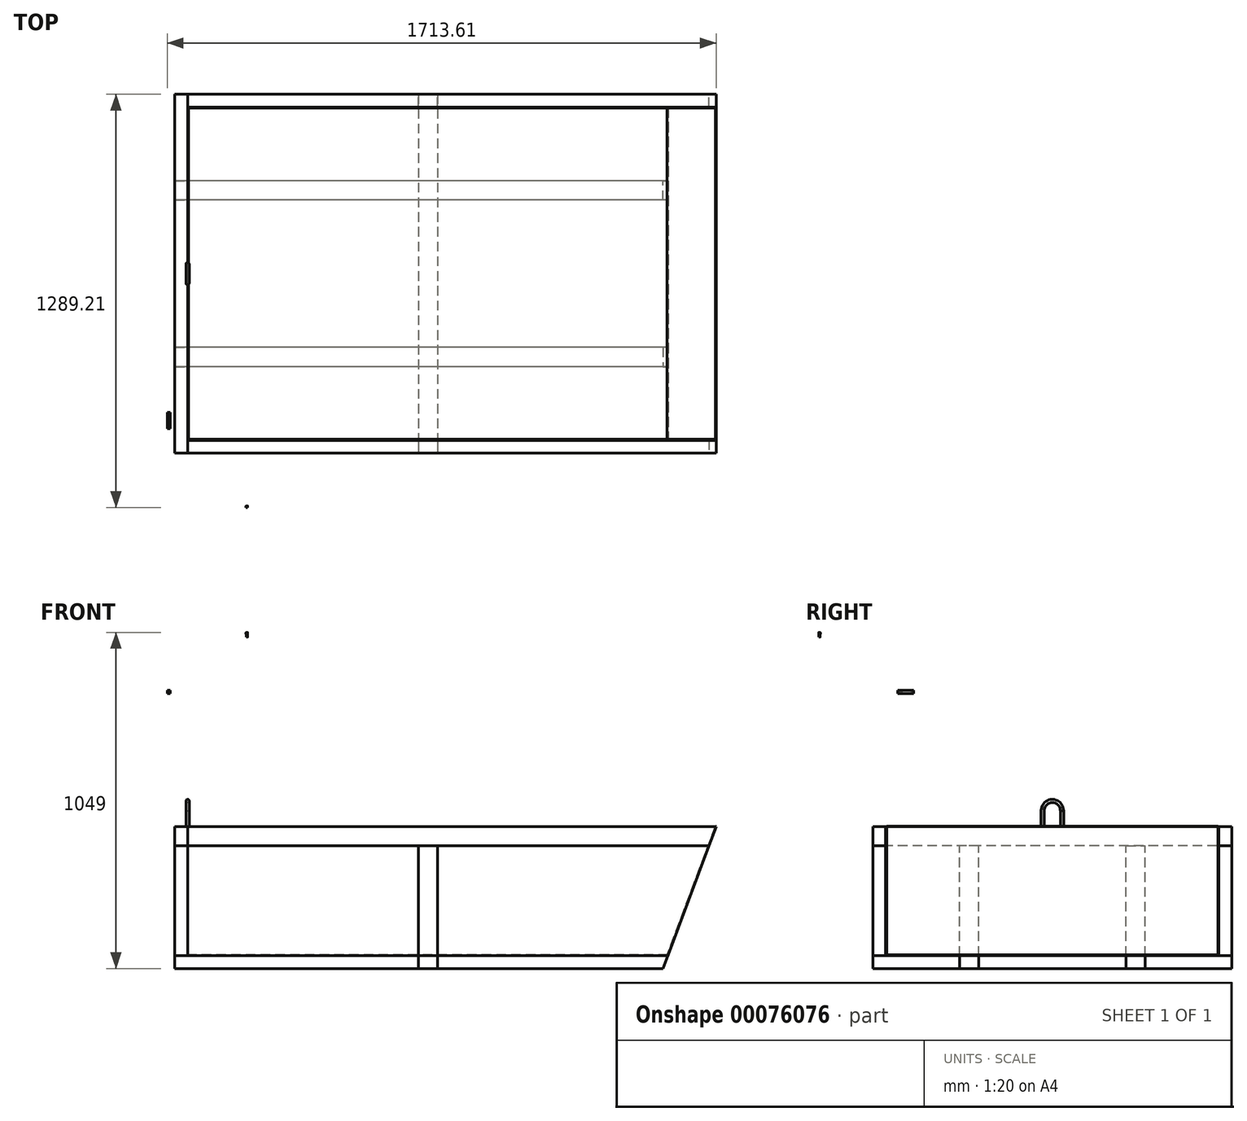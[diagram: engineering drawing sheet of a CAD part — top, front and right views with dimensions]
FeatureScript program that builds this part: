
annotation { "Feature Type Name" : "Feature", "Feature Type Description" : "" }
export const myFeature = defineFeature(function(context is Context, id is Id, definition is map)
    precondition{}
    {
        {
            var Q0;
            Q0=qCreatedBy(makeId("Top.planeOp"),FACE);
            var sketch = newSketch(context, id + "F0", { "sketchPlane" : qUnion([Q0])});
            skLineSegment(sketch, "E0.bottom", {"start": v(750, 520) * mm, "end": v(-750, 520) * mm});
            skLineSegment(sketch, "E0.top", {"start": v(750, -520) * mm, "end": v(-750, -520) * mm});
            skLineSegment(sketch, "E0.left", {"start": v(750, 520) * mm, "end": v(750, -520) * mm});
            skLineSegment(sketch, "E0.right", {"start": v(-750, 520) * mm, "end": v(-750, -520) * mm});
            skPoint(sketch, "E0.middle", {"position": v(0, 0) * mm});
            skSolve(sketch);
        }
        {
            var Q0;
            Q0 = qSketchRegion(id + "F0", true);
            extrude(context, id + "F1", {"entities" : qUnion([Q0]), "depth" : 3 * mm});
        }
        {
            var Q0;
            Q0=makeQuery(id+"F1.opExtrude","SWEPT_FACE",FACE,{"disambiguationData":[OSD([sQuery(id+"F0.wireOp",EDGE,"E0.top")])]});
            var sketch = newSketch(context, id + "F2", { "sketchPlane" : qUnion([Q0])});
            skLineSegment(sketch, "E1.0", {"start": v(750, 3) * mm, "end": v(-750, 3) * mm});
            skLineSegment(sketch, "E2", {"start": v(-750, 3) * mm, "end": v(-750, 403) * mm});
            skLineSegment(sketch, "E3", {"start": v(-750, 403) * mm, "end": v(900, 403) * mm});
            skLineSegment(sketch, "E4", {"start": v(900, 403) * mm, "end": v(750, 3) * mm});
            skSolve(sketch);
        }
        {
            var Q0;
            Q0 = qSketchRegion(id + "F2", true);
            extrude(context, id + "F3", {"entities" : qUnion([Q0]), "oppositeDirection" : true, "depth" : 3 * mm});
        }
        {
            var Q0;
            Q0=makeQuery(id+"F3.opExtrude","SWEPT_BODY",BODY,{"disambiguationData":[OSD([sQuery(id+"F2.wireOp",EDGE,"E1.0"),sQuery(id+"F2.wireOp",EDGE,"E2"),sQuery(id+"F2.wireOp",EDGE,"E3"),sQuery(id+"F2.wireOp",EDGE,"E4")])]});
            var Q1;
            Q1=qCreatedBy(makeId("Front.planeOp"),FACE);
            mirror(context, id + "F4", {"operationType" : NewBodyOperationType.ADD, "entities" : qUnion([Q0]), "mirrorPlane" : qUnion([Q1])});
        }
        {
            var Q0;
            {var subQ0=makeQuery(id+"F3.opExtrude","SWEPT_FACE",FACE,{"disambiguationData":[OSD([sQuery(id+"F2.wireOp",EDGE,"E2")])]});Q0=makeQuery(id+"F4.boolean.opBoolean","MERGE",FACE,{"derivedFrom":[makeQuery(id+"F1.opExtrude","SWEPT_FACE",FACE,{"disambiguationData":[OSD([sQuery(id+"F0.wireOp",EDGE,"E0.right")])]}),subQ0,makeQuery(id+"F4.opPattern","COPY",FACE,{"derivedFrom":subQ0,"instanceName":"1"})]});}
            var sketch = newSketch(context, id + "F5", { "sketchPlane" : qUnion([Q0])});
            skLineSegment(sketch, "E5.0", {"start": v(-517, 3) * mm, "end": v(-517, 403) * mm});
            skLineSegment(sketch, "E5.1", {"start": v(-517, 3) * mm, "end": v(517, 3) * mm});
            skLineSegment(sketch, "E5.2", {"start": v(517, 3) * mm, "end": v(517, 403) * mm});
            skLineSegment(sketch, "E6", {"start": v(-517, 403) * mm, "end": v(517, 403) * mm});
            skSolve(sketch);
        }
        {
            var Q0;
            Q0 = qSketchRegion(id + "F5", true);
            extrude(context, id + "F6", {"entities" : qUnion([Q0]), "oppositeDirection" : true, "depth" : 3 * mm});
        }
        {
            var Q0;
            Q0=makeQuery(id+"F3.opExtrude","SWEPT_FACE",FACE,{"disambiguationData":[OSD([sQuery(id+"F2.wireOp",EDGE,"E4")])]});
            var sketch = newSketch(context, id + "F7", { "sketchPlane" : qUnion([Q0])});
            skLineSegment(sketch, "E7.0", {"start": v(517, 266.15) * mm, "end": v(-517, 266.15) * mm});
            skLineSegment(sketch, "E7.1", {"start": v(-517, 693.35) * mm, "end": v(-517, 266.15) * mm});
            skLineSegment(sketch, "E7.2", {"start": v(517, 693.35) * mm, "end": v(517, 266.15) * mm});
            skLineSegment(sketch, "E8", {"start": v(-517, 693.35) * mm, "end": v(517, 693.35) * mm});
            skSolve(sketch);
        }
        {
            var Q0;
            Q0 = qSketchRegion(id + "F7", true);
            extrude(context, id + "F8", {"entities" : qUnion([Q0]), "oppositeDirection" : true, "depth" : 3 * mm});
        }
        {
            var Q0;
            Q0=makeQuery(id+"F4.boolean.opBoolean","MERGE",FACE,{"derivedFrom":[makeQuery(id+"F1.opExtrude","SWEPT_FACE",FACE,{"disambiguationData":[OSD([sQuery(id+"F0.wireOp",EDGE,"E0.top")])]}),makeQuery(id+"F3.opExtrude","CAP_FACE",FACE,{"disambiguationData":[OSD([sQuery(id+"F2.wireOp",EDGE,"E1.0"),sQuery(id+"F2.wireOp",EDGE,"E2"),sQuery(id+"F2.wireOp",EDGE,"E3"),sQuery(id+"F2.wireOp",EDGE,"E4")])],"isStart":true})]});
            cPlane(context, id + "F9", {"entities" : qUnion([Q0]), "cplaneType" : CPlaneType.OFFSET, "offset" : 40 * mm, "width" : 150 * mm, "height" : 150 * mm});
        }
        {
            var Q0;
            Q0=qCreatedBy(id+"F9.planeOp",FACE);
            var sketch = newSketch(context, id + "F10", { "sketchPlane" : qUnion([Q0])});
            skLineSegment(sketch, "E9.0", {"start": v(-750, 403) * mm, "end": v(-750, 343) * mm});
            skLineSegment(sketch, "E10", {"start": v(-750, 403) * mm, "end": v(-790, 403) * mm});
            skLineSegment(sketch, "E11", {"start": v(-790, 403) * mm, "end": v(-790, 343) * mm});
            skLineSegment(sketch, "E12", {"start": v(-790, 343) * mm, "end": v(-750, 343) * mm});
            skPoint(sketch, "E13.orphan", {"position": v(-750, 0) * mm});
            skSolve(sketch);
        }
        {
            var Q0;
            Q0 = qSketchRegion(id + "F10", true);
            extrude(context, id + "F11", {"entities" : qUnion([Q0]), "oppositeDirection" : true, "depth" : 1120 * mm});
        }
        {
            var Q0;
            Q0=makeQuery(id+"F11.opExtrude","SWEPT_FACE",FACE,{"disambiguationData":[OSD([sQuery(id+"F10.wireOp",EDGE,"E9.0")])]});
            var sketch = newSketch(context, id + "F12", { "sketchPlane" : qUnion([Q0])});
            skLineSegment(sketch, "E14.0", {"start": v(-520, 403) * mm, "end": v(-560, 403) * mm});
            skLineSegment(sketch, "E14.1", {"start": v(-560, 403) * mm, "end": v(-560, 343) * mm});
            skLineSegment(sketch, "E14.2", {"start": v(-520, 343) * mm, "end": v(-560, 343) * mm});
            skLineSegment(sketch, "E14.3", {"start": v(-520, 403) * mm, "end": v(-520, 343) * mm});
            skPoint(sketch, "E15.orphan", {"position": v(560, 403) * mm});
            skPoint(sketch, "E16.orphan", {"position": v(560, 343) * mm});
            skPoint(sketch, "E17.orphan", {"position": v(-520, 3) * mm});
            skSolve(sketch);
        }
        {
            var Q0;
            Q0=makeQuery(id+"F12.imprint","IMPRINT",FACE,{"disambiguationData":[TD([[makeQuery(id+"F12.imprint","IMPRINT",EDGE,{"derivedFrom":sQuery(id+"F12.wireOp",EDGE,"E14.0")}),1.0]])]});
            var Q1;
            Q1=makeQuery(id+"F8.opExtrude","CAP_FACE",FACE,{"disambiguationData":[OSD([sQuery(id+"F7.wireOp",EDGE,"E7.0"),sQuery(id+"F7.wireOp",EDGE,"E7.1"),sQuery(id+"F7.wireOp",EDGE,"E7.2"),sQuery(id+"F7.wireOp",EDGE,"E8")])],"isStart":true});
            extrude(context, id + "F13", {"entities" : qUnion([Q0]), "endBound" : BoundingType.UP_TO_SURFACE, "endBoundEntityFace" : qUnion([Q1]), "depth" : 25 * mm});
        }
        {
            var Q0;
            Q0=makeQuery(id+"F13.opExtrude","SWEPT_FACE",FACE,{"disambiguationData":[OSD([sQuery(id+"F12.wireOp",EDGE,"E14.2")])]});
            var sketch = newSketch(context, id + "F14", { "sketchPlane" : qUnion([Q0])});
            skLineSegment(sketch, "E18.0", {"start": v(30, 520) * mm, "end": v(-30, 520) * mm});
            skLineSegment(sketch, "E19", {"start": v(0, 520) * mm, "end": v(0, 560) * mm, "construction": true});
            skLineSegment(sketch, "E20", {"start": v(0, 560) * mm, "end": v(-30, 560) * mm});
            skLineSegment(sketch, "E21", {"start": v(-30, 560) * mm, "end": v(-30, 520) * mm});
            skLineSegment(sketch, "E22", {"start": v(0, 560) * mm, "end": v(30, 560) * mm});
            skLineSegment(sketch, "E23", {"start": v(30, 560) * mm, "end": v(30, 520) * mm});
            skPoint(sketch, "E24.orphan", {"position": v(-750, 520) * mm});
            skPoint(sketch, "E25.orphan", {"position": v(750, 520) * mm});
            skSolve(sketch);
        }
        {
            var Q0;
            Q0 = qSketchRegion(id + "F14", true);
            var Q1;
            Q1=makeQuery(id+"F1.opExtrude","CAP_FACE",FACE,{"disambiguationData":[OSD([sQuery(id+"F0.wireOp",EDGE,"E0.bottom"),sQuery(id+"F0.wireOp",EDGE,"E0.top"),sQuery(id+"F0.wireOp",EDGE,"E0.left"),sQuery(id+"F0.wireOp",EDGE,"E0.right")])],"isStart":true});
            extrude(context, id + "F15", {"entities" : qUnion([Q0]), "endBound" : BoundingType.UP_TO_SURFACE, "endBoundEntityFace" : qUnion([Q1]), "depth" : 25 * mm});
        }
        {
            var Q0;
            Q0=makeQuery(id+"F11.opExtrude","SWEPT_FACE",FACE,{"disambiguationData":[OSD([sQuery(id+"F10.wireOp",EDGE,"E12")])]});
            var sketch = newSketch(context, id + "F16", { "sketchPlane" : qUnion([Q0])});
            skLineSegment(sketch, "E26.0", {"start": v(-750, 230) * mm, "end": v(-750, 290) * mm});
            skLineSegment(sketch, "E27.bottom", {"start": v(-750, 230) * mm, "end": v(-790, 230) * mm});
            skLineSegment(sketch, "E27.top", {"start": v(-750, 290) * mm, "end": v(-790, 290) * mm});
            skLineSegment(sketch, "E27.right", {"start": v(-790, 230) * mm, "end": v(-790, 290) * mm});
            skPoint(sketch, "E28.orphan", {"position": v(-750, -520) * mm});
            skPoint(sketch, "E29.orphan", {"position": v(-750, 520) * mm});
            skSolve(sketch);
        }
        {
            var Q0;
            Q0 = qSketchRegion(id + "F16", true);
            var Q1;
            Q1=makeQuery(id+"F1.opExtrude","CAP_FACE",FACE,{"disambiguationData":[OSD([sQuery(id+"F0.wireOp",EDGE,"E0.bottom"),sQuery(id+"F0.wireOp",EDGE,"E0.top"),sQuery(id+"F0.wireOp",EDGE,"E0.left"),sQuery(id+"F0.wireOp",EDGE,"E0.right")])],"isStart":true});
            extrude(context, id + "F17", {"entities" : qUnion([Q0]), "endBound" : BoundingType.UP_TO_SURFACE, "endBoundEntityFace" : qUnion([Q1]), "depth" : 25 * mm});
        }
        {
            var Q0;
            Q0=makeQuery(id+"F17.opExtrude","SWEPT_FACE",FACE,{"disambiguationData":[OSD([sQuery(id+"F16.wireOp",EDGE,"E27.right")])]});
            var sketch = newSketch(context, id + "F18", { "sketchPlane" : qUnion([Q0])});
            skLineSegment(sketch, "E30.0", {"start": v(290, 0) * mm, "end": v(230, 0) * mm});
            skLineSegment(sketch, "E31", {"start": v(230, 0) * mm, "end": v(230, -40) * mm});
            skLineSegment(sketch, "E32", {"start": v(230, -40) * mm, "end": v(290, -40) * mm});
            skLineSegment(sketch, "E33", {"start": v(290, -40) * mm, "end": v(290, 0) * mm});
            skSolve(sketch);
        }
        {
            var Q0;
            Q0 = qSketchRegion(id + "F18", true);
            var Q1;
            Q1=makeQuery(id+"F8.opExtrude","CAP_FACE",FACE,{"disambiguationData":[OSD([sQuery(id+"F7.wireOp",EDGE,"E7.0"),sQuery(id+"F7.wireOp",EDGE,"E7.1"),sQuery(id+"F7.wireOp",EDGE,"E7.2"),sQuery(id+"F7.wireOp",EDGE,"E8")])],"isStart":true});
            extrude(context, id + "F19", {"entities" : qUnion([Q0]), "endBound" : BoundingType.UP_TO_SURFACE, "oppositeDirection" : true, "endBoundEntityFace" : qUnion([Q1]), "depth" : 25 * mm});
        }
        {
            var Q0;
            Q0=makeQuery(id+"F13.opExtrude","SWEPT_BODY",BODY,{"disambiguationData":[OSD([sQuery(id+"F12.wireOp",EDGE,"E14.0"),sQuery(id+"F12.wireOp",EDGE,"E14.1"),sQuery(id+"F12.wireOp",EDGE,"E14.2"),sQuery(id+"F12.wireOp",EDGE,"E14.3")])]});
            var Q1;
            Q1=makeQuery(id+"F15.opExtrude","SWEPT_BODY",BODY,{"disambiguationData":[OSD([sQuery(id+"F14.wireOp",EDGE,"E18.0"),sQuery(id+"F14.wireOp",EDGE,"E20"),sQuery(id+"F14.wireOp",EDGE,"E21"),sQuery(id+"F14.wireOp",EDGE,"E22"),sQuery(id+"F14.wireOp",EDGE,"E23")])]});
            var Q2;
            Q2=makeQuery(id+"F17.opExtrude","SWEPT_BODY",BODY,{"disambiguationData":[OSD([sQuery(id+"F16.wireOp",EDGE,"E27.bottom"),sQuery(id+"F16.wireOp",EDGE,"E27.top"),sQuery(id+"F16.wireOp",EDGE,"E26.0"),sQuery(id+"F16.wireOp",EDGE,"E27.right")])]});
            var Q3;
            Q3=makeQuery(id+"F19.opExtrude","SWEPT_BODY",BODY,{"disambiguationData":[OSD([sQuery(id+"F18.wireOp",EDGE,"E30.0"),sQuery(id+"F18.wireOp",EDGE,"E31"),sQuery(id+"F18.wireOp",EDGE,"E32"),sQuery(id+"F18.wireOp",EDGE,"E33")])]});
            var Q4;
            Q4=qCreatedBy(makeId("Front.planeOp"),FACE);
            mirror(context, id + "F20", {"entities" : qUnion([Q0, Q1, Q2, Q3]), "mirrorPlane" : qUnion([Q4])});
        }
        {
            var Q0;
            Q0=makeQuery(id+"F15.opExtrude","SWEPT_FACE",FACE,{"disambiguationData":[OSD([sQuery(id+"F14.wireOp",EDGE,"E20"),sQuery(id+"F14.wireOp",EDGE,"E22")])]});
            var sketch = newSketch(context, id + "F21", { "sketchPlane" : qUnion([Q0])});
            skLineSegment(sketch, "E34.0", {"start": v(-30, 0) * mm, "end": v(30, 0) * mm});
            skLineSegment(sketch, "E35.0", {"start": v(30, -40) * mm, "end": v(-30, -40) * mm});
            skLineSegment(sketch, "E36", {"start": v(-30, 0) * mm, "end": v(-30, -40) * mm});
            skLineSegment(sketch, "E37", {"start": v(30, 0) * mm, "end": v(30, -40) * mm});
            skPoint(sketch, "E38.orphan", {"position": v(-790, -40) * mm});
            skPoint(sketch, "E39.orphan", {"position": v(733.87, -40) * mm});
            skSolve(sketch);
        }
        {
            var Q0;
            Q0 = qSketchRegion(id + "F21", true);
            var Q1;
            Q1=makeQuery(id+"F20.opPattern","COPY",FACE,{"derivedFrom":makeQuery(id+"F15.opExtrude","SWEPT_FACE",FACE,{"disambiguationData":[OSD([sQuery(id+"F14.wireOp",EDGE,"E20"),sQuery(id+"F14.wireOp",EDGE,"E22")])]}),"instanceName":"1"});
            extrude(context, id + "F22", {"entities" : qUnion([Q0]), "endBound" : BoundingType.UP_TO_SURFACE, "oppositeDirection" : true, "endBoundEntityFace" : qUnion([Q1]), "depth" : 25 * mm});
        }
        {
            var Q0;
            Q0=makeQuery(id+"F6.opExtrude","CAP_FACE",FACE,{"disambiguationData":[OSD([sQuery(id+"F5.wireOp",EDGE,"E5.0"),sQuery(id+"F5.wireOp",EDGE,"E5.1"),sQuery(id+"F5.wireOp",EDGE,"E5.2"),sQuery(id+"F5.wireOp",EDGE,"E6")])],"isStart":true});
            var sketch = newSketch(context, id + "F23", { "sketchPlane" : qUnion([Q0])});
            skLineSegment(sketch, "E40.0", {"start": v(-30, 403) * mm, "end": v(30, 403) * mm, "construction": true});
            skPoint(sketch, "E41.endSnap0", {"position": v(0, 403) * mm});
            skArc(sketch, "E42", {"start": v(30, 453) * mm, "mid": v(-0.26, 483) * mm, "end": v(-30, 452.48) * mm});
            skLineSegment(sketch, "E43", {"start": v(-30, 452.48) * mm, "end": v(-30, 403) * mm});
            skLineSegment(sketch, "E44", {"start": v(30, 453) * mm, "end": v(30, 403) * mm});
            skPoint(sketch, "E45.orphan", {"position": v(560, 403) * mm});
            skPoint(sketch, "E46.orphan", {"position": v(-560, 403) * mm});
            skSolve(sketch);
        }
        {
            var Q0;
            Q0=makeQuery(id+"F11.opExtrude","SWEPT_FACE",FACE,{"disambiguationData":[OSD([sQuery(id+"F10.wireOp",EDGE,"E10")])]});
            var sketch = newSketch(context, id + "F24", { "sketchPlane" : qUnion([Q0])});
            skLineSegment(sketch, "E47.0", {"start": v(-750, 30) * mm, "end": v(-750, -30) * mm, "construction": true});
            skCircle(sketch, "E48", {"center": v(-750, 30) * mm, "radius": 5 * mm});
            skSolve(sketch);
        }
        {
            var Q0;
            {var subQ0=sQuery(id+"F24.wireOp",EDGE,"E48");var subQ1=makeQuery(id+"F11.opExtrude","SWEPT_EDGE",EDGE,{"disambiguationData":[OSD([sQuery(id+"F10.wireOp",EDGE,"E9.0"),sQuery(id+"F10.wireOp",EDGE,"E10")])]});var subQ2=makeQuery(id+"F24.imprint","INTERSECT",VERTEX,{"disambiguationData":[OD(0.0)],"derivedFrom":[subQ1,subQ0]});Q0=makeQuery(id+"F24.imprint","IMPRINT",FACE,{"disambiguationData":[TD([[makeQuery(id+"F24.imprint","IMPRINT",EDGE,{"disambiguationData":[TD([[subQ2,1.0]])],"derivedFrom":subQ0}),1.0]])]});}
            var Q1;
            {var subQ0=sQuery(id+"F24.wireOp",EDGE,"E48");var subQ1=makeQuery(id+"F11.opExtrude","SWEPT_EDGE",EDGE,{"disambiguationData":[OSD([sQuery(id+"F10.wireOp",EDGE,"E9.0"),sQuery(id+"F10.wireOp",EDGE,"E10")])]});var subQ2=makeQuery(id+"F24.imprint","INTERSECT",VERTEX,{"disambiguationData":[OD(0.0)],"derivedFrom":[subQ1,subQ0]});Q1=makeQuery(id+"F24.imprint","IMPRINT",FACE,{"disambiguationData":[TD([[makeQuery(id+"F24.imprint","IMPRINT",EDGE,{"disambiguationData":[TD([[subQ2,-1.0]])],"derivedFrom":subQ0}),1.0]])]});}
            var Q2;
            Q2=sQuery(id+"F23.wireOp",EDGE,"E43");
            var Q3;
            Q3=sQuery(id+"F23.wireOp",EDGE,"E42");
            var Q4;
            Q4=sQuery(id+"F23.wireOp",EDGE,"E44");
            sweep(context, id + "F25", {"profiles" : qUnion([Q0, Q1]), "path" : qUnion([Q2, Q3, Q4])});
        }
        {
            var Q0;
            Q0=makeQuery(id+"F1.opExtrude","CAP_FACE",FACE,{"disambiguationData":[OSD([sQuery(id+"F0.wireOp",EDGE,"E0.bottom"),sQuery(id+"F0.wireOp",EDGE,"E0.top"),sQuery(id+"F0.wireOp",EDGE,"E0.left"),sQuery(id+"F0.wireOp",EDGE,"E0.right")])],"isStart":false});
            cPlane(context, id + "F26", {"entities" : qUnion([Q0]), "cplaneType" : CPlaneType.OFFSET, "offset" : 1000 * mm, "width" : 150 * mm, "height" : 150 * mm});
        }
        {
            var Q0;
            Q0=makeQuery(id+"F4.opPattern","COPY",FACE,{"derivedFrom":makeQuery(id+"F3.opExtrude","CAP_FACE",FACE,{"disambiguationData":[OSD([sQuery(id+"F2.wireOp",EDGE,"E1.0"),sQuery(id+"F2.wireOp",EDGE,"E2"),sQuery(id+"F2.wireOp",EDGE,"E3"),sQuery(id+"F2.wireOp",EDGE,"E4")])],"isStart":false}),"instanceName":"1"});
            cPlane(context, id + "F27", {"entities" : qUnion([Q0]), "cplaneType" : CPlaneType.OFFSET, "offset" : 1000 * mm, "width" : 150 * mm, "height" : 150 * mm});
        }
        {
            var Q0;
            Q0=qCreatedBy(id+"F27.planeOp",FACE);
            var sketch = newSketch(context, id + "F28", { "sketchPlane" : qUnion([Q0])});
            skLineSegment(sketch, "E49.bottom", {"start": v(-813.61, 828.05) * mm, "end": v(-803.61, 828.05) * mm});
            skLineSegment(sketch, "E49.top", {"start": v(-813.61, 818.05) * mm, "end": v(-803.61, 818.05) * mm});
            skLineSegment(sketch, "E49.left", {"start": v(-813.61, 828.05) * mm, "end": v(-813.61, 818.05) * mm});
            skLineSegment(sketch, "E49.right", {"start": v(-803.61, 828.05) * mm, "end": v(-803.61, 818.05) * mm});
            skCircle(sketch, "E50", {"center": v(-808.61, 823.05) * mm, "radius": 1.65 * mm});
            skPoint(sketch, "E50.centerSnap0", {"position": v(-813.61, 823.05) * mm});
            skPoint(sketch, "E50.centerSnap1", {"position": v(-808.61, 828.05) * mm});
            skSolve(sketch);
        }
        {
            var Q0;
            Q0=makeQuery(id+"F28.imprint","IMPRINT",FACE,{"disambiguationData":[TD([[makeQuery(id+"F28.imprint","IMPRINT",EDGE,{"derivedFrom":sQuery(id+"F28.wireOp",EDGE,"E49.bottom")}),-1.0]])]});
            var Q1;
            Q1=makeQuery(id+"F28.imprint","IMPRINT",FACE,{"disambiguationData":[TD([[makeQuery(id+"F28.imprint","IMPRINT",EDGE,{"derivedFrom":sQuery(id+"F28.wireOp",EDGE,"E50")}),1.0]])]});
            extrude(context, id + "F29", {"entities" : qUnion([Q0, Q1]), "oppositeDirection" : true, "depth" : 50 * mm});
        }
        {
            var Q0;
            Q0=makeQuery(id+"F28.imprint","IMPRINT",FACE,{"disambiguationData":[TD([[makeQuery(id+"F28.imprint","IMPRINT",EDGE,{"derivedFrom":sQuery(id+"F28.wireOp",EDGE,"E50")}),1.0]])]});
            extrude(context, id + "F30", {"entities" : qUnion([Q0]), "operationType" : NewBodyOperationType.REMOVE, "oppositeDirection" : true, "depth" : 15 * mm});
        }
        {
            var Q0;
            Q0=makeQuery(id+"F29.opExtrude","SWEPT_FACE",FACE,{"disambiguationData":[OSD([sQuery(id+"F28.wireOp",EDGE,"E49.bottom")])]});
            var sketch = newSketch(context, id + "F31", { "sketchPlane" : qUnion([Q0])});
            skCircle(sketch, "E51", {"center": v(-808.61, -437.5) * mm, "radius": 2.05 * mm});
            skPoint(sketch, "E51.centerSnap0", {"position": v(-808.61, -433) * mm});
            skSolve(sketch);
        }
        {
            var Q0;
            Q0=makeQuery(id+"F31.imprint","IMPRINT",FACE,{"disambiguationData":[TD([[makeQuery(id+"F31.imprint","IMPRINT",EDGE,{"derivedFrom":sQuery(id+"F31.wireOp",EDGE,"E51")}),1.0]])]});
            extrude(context, id + "F32", {"entities" : qUnion([Q0]), "operationType" : NewBodyOperationType.REMOVE, "endBound" : BoundingType.THROUGH_ALL, "oppositeDirection" : true, "depth" : 25 * mm});
        }
        {
            var Q0;
            Q0=qCreatedBy(id+"F26.planeOp",FACE);
            var sketch = newSketch(context, id + "F33", { "sketchPlane" : qUnion([Q0])});
            skLineSegment(sketch, "E52.bottom", {"start": v(-567.25, -724.2) * mm, "end": v(-562.25, -724.2) * mm});
            skLineSegment(sketch, "E52.top", {"start": v(-567.25, -729.2) * mm, "end": v(-562.25, -729.2) * mm});
            skLineSegment(sketch, "E52.left", {"start": v(-567.25, -724.2) * mm, "end": v(-567.25, -729.2) * mm});
            skLineSegment(sketch, "E52.right", {"start": v(-562.25, -724.2) * mm, "end": v(-562.25, -729.2) * mm});
            skCircle(sketch, "E53", {"center": v(-564.75, -726.7) * mm, "radius": 2 * mm});
            skPoint(sketch, "E53.centerSnap0", {"position": v(-564.75, -724.2) * mm});
            skPoint(sketch, "E53.centerSnap1", {"position": v(-567.25, -726.7) * mm});
            skSolve(sketch);
        }
        {
            var Q0;
            Q0=makeQuery(id+"F33.imprint","IMPRINT",FACE,{"disambiguationData":[TD([[makeQuery(id+"F33.imprint","IMPRINT",EDGE,{"derivedFrom":sQuery(id+"F33.wireOp",EDGE,"E52.bottom")}),-1.0]])]});
            var Q1;
            Q1=makeQuery(id+"F33.imprint","IMPRINT",FACE,{"disambiguationData":[TD([[makeQuery(id+"F33.imprint","IMPRINT",EDGE,{"derivedFrom":sQuery(id+"F33.wireOp",EDGE,"E53")}),1.0]])]});
            extrude(context, id + "F34", {"entities" : qUnion([Q0, Q1]), "depth" : 6 * mm});
        }
        {
            var Q0;
            Q0=makeQuery(id+"F33.imprint","IMPRINT",FACE,{"disambiguationData":[TD([[makeQuery(id+"F33.imprint","IMPRINT",EDGE,{"derivedFrom":sQuery(id+"F33.wireOp",EDGE,"E53")}),1.0]])]});
            extrude(context, id + "F35", {"entities" : qUnion([Q0]), "operationType" : NewBodyOperationType.ADD, "oppositeDirection" : true, "depth" : 9 * mm});
        }
        {
            var Q0;
            Q0=makeQuery(id+"F34.opExtrude","CAP_EDGE",EDGE,{"disambiguationData":[OSD([sQuery(id+"F33.wireOp",EDGE,"E52.top")])],"isStart":false});
            var Q1;
            Q1=makeQuery(id+"F34.opExtrude","CAP_EDGE",EDGE,{"disambiguationData":[OSD([sQuery(id+"F33.wireOp",EDGE,"E52.right")])],"isStart":false});
            var Q2;
            Q2=makeQuery(id+"F34.opExtrude","CAP_EDGE",EDGE,{"disambiguationData":[OSD([sQuery(id+"F33.wireOp",EDGE,"E52.bottom")])],"isStart":false});
            var Q3;
            Q3=makeQuery(id+"F34.opExtrude","CAP_EDGE",EDGE,{"disambiguationData":[OSD([sQuery(id+"F33.wireOp",EDGE,"E52.left")])],"isStart":false});
            fillet(context, id + "F36", {"entities" : qUnion([Q0, Q1, Q2, Q3]), "radius" : 0.5 * mm, "tangentPropagation" : true, "allowEdgeOverflow" : false});
        }
        {
            var Q0;
            Q0=qCreatedBy(makeId("Top.planeOp"),FACE);
            cPlane(context, id + "F37", {"entities" : qUnion([Q0]), "cplaneType" : CPlaneType.OFFSET, "offset" : 730 * mm, "width" : 150 * mm, "height" : 150 * mm});
        }
        {
            var Q0;
            Q0=qCreatedBy(id+"F37.planeOp",FACE);
            var sketch = newSketch(context, id + "F38", { "sketchPlane" : qUnion([Q0])});
            skLineSegment(sketch, "E54", {"start": v(0, 0) * mm, "end": v(0, 300) * mm, "construction": true});
            skLineSegment(sketch, "E55", {"start": v(0, 300) * mm, "end": v(-600, 300) * mm, "construction": true});
            skSolve(sketch);
        }
    });
